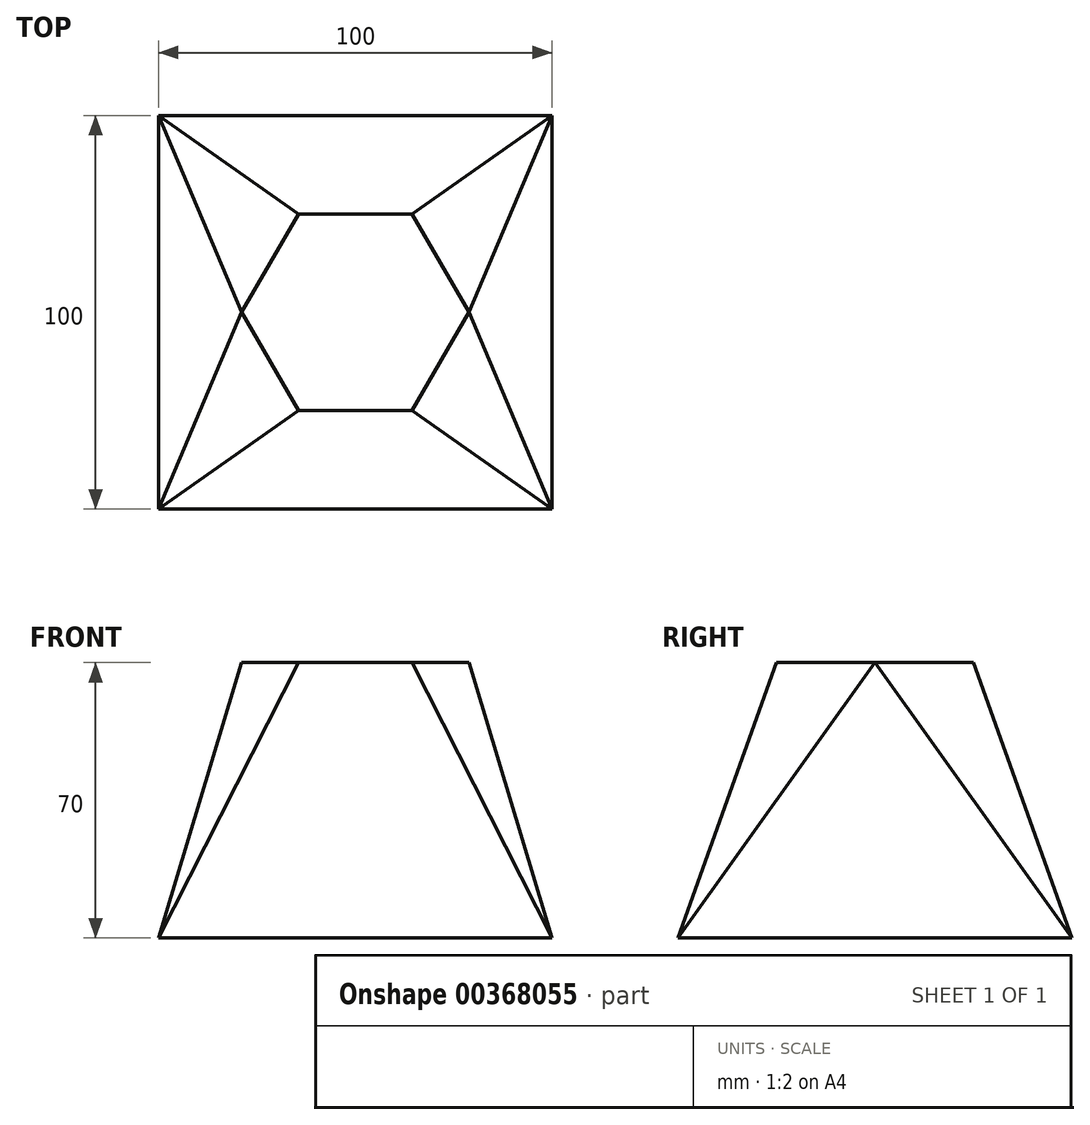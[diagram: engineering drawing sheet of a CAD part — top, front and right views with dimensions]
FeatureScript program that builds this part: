
annotation { "Feature Type Name" : "Feature", "Feature Type Description" : "" }
export const myFeature = defineFeature(function(context is Context, id is Id, definition is map)
    precondition{}
    {
        {
            var Q0;
            Q0=qCreatedBy(makeId("Top.planeOp"),FACE);
            var sketch = newSketch(context, id + "F0", { "sketchPlane" : qUnion([Q0])});
            skLineSegment(sketch, "E0.bottom", {"start": v(50, -50) * mm, "end": v(-50, -50) * mm});
            skLineSegment(sketch, "E0.top", {"start": v(50, 50) * mm, "end": v(-50, 50) * mm});
            skLineSegment(sketch, "E0.left", {"start": v(50, -50) * mm, "end": v(50, 50) * mm});
            skLineSegment(sketch, "E0.right", {"start": v(-50, -50) * mm, "end": v(-50, 50) * mm});
            skPoint(sketch, "E0.middle", {"position": v(0, 0) * mm});
            skSolve(sketch);
        }
        {
            var Q0;
            Q0=qCreatedBy(makeId("Top.planeOp"),FACE);
            cPlane(context, id + "F1", {"entities" : qUnion([Q0]), "cplaneType" : CPlaneType.OFFSET, "offset" : 70 * mm, "width" : 150 * mm, "height" : 150 * mm});
        }
        {
            var Q0;
            Q0=qCreatedBy(id+"F1.planeOp",FACE);
            var sketch = newSketch(context, id + "F2", { "sketchPlane" : qUnion([Q0])});
            skCircle(sketch, "E1.cCircle", {"center": v(0, 0) * mm, "radius": 25 * mm, "construction": true});
            skLineSegment(sketch, "E1.0", {"start": v(14.43, -25) * mm, "end": v(-14.43, -25) * mm});
            skLineSegment(sketch, "E1.1", {"start": v(-14.43, -25) * mm, "end": v(-28.87, 0) * mm});
            skLineSegment(sketch, "E1.2", {"start": v(-28.87, 0) * mm, "end": v(-14.43, 25) * mm});
            skLineSegment(sketch, "E1.3", {"start": v(-14.43, 25) * mm, "end": v(14.43, 25) * mm});
            skLineSegment(sketch, "E1.4", {"start": v(14.43, 25) * mm, "end": v(28.87, 0) * mm});
            skLineSegment(sketch, "E1.5", {"start": v(28.87, 0) * mm, "end": v(14.43, -25) * mm});
            skPoint(sketch, "E1.0.midPoint", {"position": v(0, -25) * mm});
            skLineSegment(sketch, "E2", {"start": v(-14.43, 25) * mm, "end": v(-14.43, -25) * mm});
            skLineSegment(sketch, "E3", {"start": v(14.43, 25) * mm, "end": v(14.43, -25) * mm});
            skSolve(sketch);
        }
        {
            var Q0;
            Q0=makeQuery(id+"F2.imprint","IMPRINT",FACE,{"disambiguationData":[TD([[makeQuery(id+"F2.imprint","IMPRINT",EDGE,{"derivedFrom":sQuery(id+"F2.wireOp",EDGE,"E1.0")}),-1.0]])]});
            var Q1;
            Q1=makeQuery(id+"F0.imprint","IMPRINT",FACE,{"disambiguationData":[TD([[makeQuery(id+"F0.imprint","IMPRINT",EDGE,{"derivedFrom":sQuery(id+"F0.wireOp",EDGE,"E0.bottom")}),-1.0]])]});
            loft(context, id + "F3", {"sheetProfilesArray" : [{ "sheetProfileEntities" : qUnion([Q0]) }, { "sheetProfileEntities" : qUnion([Q1]) }]});
        }
        {
            var Q1;
            Q1=makeQuery(id+"F2.imprint","IMPRINT",FACE,{"disambiguationData":[TD([[makeQuery(id+"F2.imprint","IMPRINT",EDGE,{"derivedFrom":sQuery(id+"F2.wireOp",EDGE,"E1.4")}),-1.0]])]});
            var Q2;
            Q2=makeQuery(id+"F3.opLoft","MID_CAP_VERTEX",VERTEX,{"disambiguationData":[OSD([sQuery(id+"F0.wireOp",EDGE,"E0.bottom"),sQuery(id+"F0.wireOp",EDGE,"E0.left")])],"capPos":1.0});
            loft(context, id + "F4", {"operationType" : NewBodyOperationType.ADD, "sheetProfilesArray" : [{ "sheetProfileEntities" : qUnion([Q1]) }, { "sheetProfileEntities" : qUnion([Q2]) }]});
        }
        {
            var Q1;
            Q1=makeQuery(id+"F2.imprint","IMPRINT",FACE,{"disambiguationData":[TD([[makeQuery(id+"F2.imprint","IMPRINT",EDGE,{"derivedFrom":sQuery(id+"F2.wireOp",EDGE,"E1.4")}),-1.0]])]});
            var Q2;
            Q2=makeQuery(id+"F3.opLoft","MID_CAP_VERTEX",VERTEX,{"disambiguationData":[OSD([sQuery(id+"F0.wireOp",EDGE,"E0.top"),sQuery(id+"F0.wireOp",EDGE,"E0.left")])],"capPos":1.0});
            loft(context, id + "F5", {"operationType" : NewBodyOperationType.ADD, "sheetProfilesArray" : [{ "sheetProfileEntities" : qUnion([Q1]) }, { "sheetProfileEntities" : qUnion([Q2]) }]});
        }
        {
            var Q1;
            Q1=makeQuery(id+"F5.opLoft","SWEPT_FACE",FACE,{"disambiguationData":[OSD([sQuery(id+"F2.wireOp",EDGE,"E1.0"),sQuery(id+"F2.wireOp",EDGE,"E1.4"),sQuery(id+"F2.wireOp",EDGE,"E1.5"),sQuery(id+"F2.wireOp",EDGE,"E3")])]});
            var Q2;
            Q2=makeQuery(id+"F4.opLoft","SWEPT_FACE",FACE,{"disambiguationData":[OSD([sQuery(id+"F2.wireOp",EDGE,"E1.3"),sQuery(id+"F2.wireOp",EDGE,"E1.4"),sQuery(id+"F2.wireOp",EDGE,"E1.5"),sQuery(id+"F2.wireOp",EDGE,"E3")])]});
            var Q3;
            {var subQ0=sQuery(id+"F0.wireOp",EDGE,"E0.left");var subQ1=sQuery(id+"F0.wireOp",EDGE,"E0.top");Q3=makeQuery(id+"F5.boolean.opBoolean","MERGE",VERTEX,{"derivedFrom":[makeQuery(id+"F3.opLoft","MID_CAP_VERTEX",VERTEX,{"disambiguationData":[OSD([subQ1,subQ0])],"capPos":1.0}),makeQuery(id+"F5.opLoft","SWEPT_VERTEX",VERTEX,{"disambiguationData":[OSD([subQ1,subQ0,sQuery(id+"F2.wireOp",EDGE,"E1.3"),sQuery(id+"F2.wireOp",EDGE,"E1.4"),sQuery(id+"F2.wireOp",EDGE,"E3")])]})]});}
            var Q4;
            {var subQ0=sQuery(id+"F0.wireOp",EDGE,"E0.left");var subQ1=sQuery(id+"F0.wireOp",EDGE,"E0.bottom");Q4=makeQuery(id+"F4.boolean.opBoolean","MERGE",VERTEX,{"derivedFrom":[makeQuery(id+"F3.opLoft","MID_CAP_VERTEX",VERTEX,{"disambiguationData":[OSD([subQ1,subQ0])],"capPos":1.0}),makeQuery(id+"F4.opLoft","SWEPT_VERTEX",VERTEX,{"disambiguationData":[OSD([subQ1,subQ0,sQuery(id+"F2.wireOp",EDGE,"E1.3"),sQuery(id+"F2.wireOp",EDGE,"E1.4"),sQuery(id+"F2.wireOp",EDGE,"E3")])]})]});}
            loft(context, id + "F6", {"operationType" : NewBodyOperationType.ADD, "sheetProfilesArray" : [{ "sheetProfileEntities" : qUnion([Q1]) }, { "sheetProfileEntities" : qUnion([Q2]) }], "matchConnections" : true, "connections" : [{ "connectionEntities" : qUnion([Q3, Q4]), "connectionEdgeQueries" : qUnion([]), "connectionEdgeParameters" : [] }]});
        }
        {
            var Q1;
            Q1=makeQuery(id+"F2.imprint","IMPRINT",FACE,{"disambiguationData":[TD([[makeQuery(id+"F2.imprint","IMPRINT",EDGE,{"derivedFrom":sQuery(id+"F2.wireOp",EDGE,"E1.1")}),-1.0]])]});
            var Q2;
            Q2=makeQuery(id+"F3.opLoft","MID_CAP_VERTEX",VERTEX,{"disambiguationData":[OSD([sQuery(id+"F0.wireOp",EDGE,"E0.bottom"),sQuery(id+"F0.wireOp",EDGE,"E0.right")])],"capPos":1.0});
            loft(context, id + "F7", {"operationType" : NewBodyOperationType.ADD, "sheetProfilesArray" : [{ "sheetProfileEntities" : qUnion([Q1]) }, { "sheetProfileEntities" : qUnion([Q2]) }]});
        }
        {
            var Q1;
            Q1=makeQuery(id+"F2.imprint","IMPRINT",FACE,{"disambiguationData":[TD([[makeQuery(id+"F2.imprint","IMPRINT",EDGE,{"derivedFrom":sQuery(id+"F2.wireOp",EDGE,"E1.1")}),-1.0]])]});
            var Q2;
            Q2=makeQuery(id+"F3.opLoft","MID_CAP_VERTEX",VERTEX,{"disambiguationData":[OSD([sQuery(id+"F0.wireOp",EDGE,"E0.top"),sQuery(id+"F0.wireOp",EDGE,"E0.right")])],"capPos":1.0});
            loft(context, id + "F8", {"operationType" : NewBodyOperationType.ADD, "sheetProfilesArray" : [{ "sheetProfileEntities" : qUnion([Q1]) }, { "sheetProfileEntities" : qUnion([Q2]) }]});
        }
        {
            var Q1;
            Q1=makeQuery(id+"F8.opLoft","SWEPT_FACE",FACE,{"disambiguationData":[OSD([sQuery(id+"F2.wireOp",EDGE,"E1.0"),sQuery(id+"F2.wireOp",EDGE,"E1.1"),sQuery(id+"F2.wireOp",EDGE,"E1.2"),sQuery(id+"F2.wireOp",EDGE,"E2")])]});
            var Q2;
            Q2=makeQuery(id+"F7.opLoft","SWEPT_FACE",FACE,{"disambiguationData":[OSD([sQuery(id+"F2.wireOp",EDGE,"E1.1"),sQuery(id+"F2.wireOp",EDGE,"E1.2"),sQuery(id+"F2.wireOp",EDGE,"E1.3"),sQuery(id+"F2.wireOp",EDGE,"E2")])]});
            var Q3;
            {var subQ0=sQuery(id+"F0.wireOp",EDGE,"E0.right");var subQ1=sQuery(id+"F0.wireOp",EDGE,"E0.top");Q3=makeQuery(id+"F8.boolean.opBoolean","MERGE",VERTEX,{"derivedFrom":[makeQuery(id+"F3.opLoft","MID_CAP_VERTEX",VERTEX,{"disambiguationData":[OSD([subQ1,subQ0])],"capPos":1.0}),makeQuery(id+"F8.opLoft","SWEPT_VERTEX",VERTEX,{"disambiguationData":[OSD([subQ1,subQ0,sQuery(id+"F2.wireOp",EDGE,"E1.1"),sQuery(id+"F2.wireOp",EDGE,"E1.2")])]})]});}
            var Q4;
            {var subQ0=sQuery(id+"F0.wireOp",EDGE,"E0.right");var subQ1=sQuery(id+"F0.wireOp",EDGE,"E0.bottom");Q4=makeQuery(id+"F7.boolean.opBoolean","MERGE",VERTEX,{"derivedFrom":[makeQuery(id+"F3.opLoft","MID_CAP_VERTEX",VERTEX,{"disambiguationData":[OSD([subQ1,subQ0])],"capPos":1.0}),makeQuery(id+"F7.opLoft","SWEPT_VERTEX",VERTEX,{"disambiguationData":[OSD([subQ1,subQ0,sQuery(id+"F2.wireOp",EDGE,"E1.1"),sQuery(id+"F2.wireOp",EDGE,"E1.2")])]})]});}
            loft(context, id + "F9", {"operationType" : NewBodyOperationType.ADD, "sheetProfilesArray" : [{ "sheetProfileEntities" : qUnion([Q1]) }, { "sheetProfileEntities" : qUnion([Q2]) }], "matchConnections" : true, "connections" : [{ "connectionEntities" : qUnion([Q3, Q4]), "connectionEdgeQueries" : qUnion([]), "connectionEdgeParameters" : [] }]});
        }
    });
